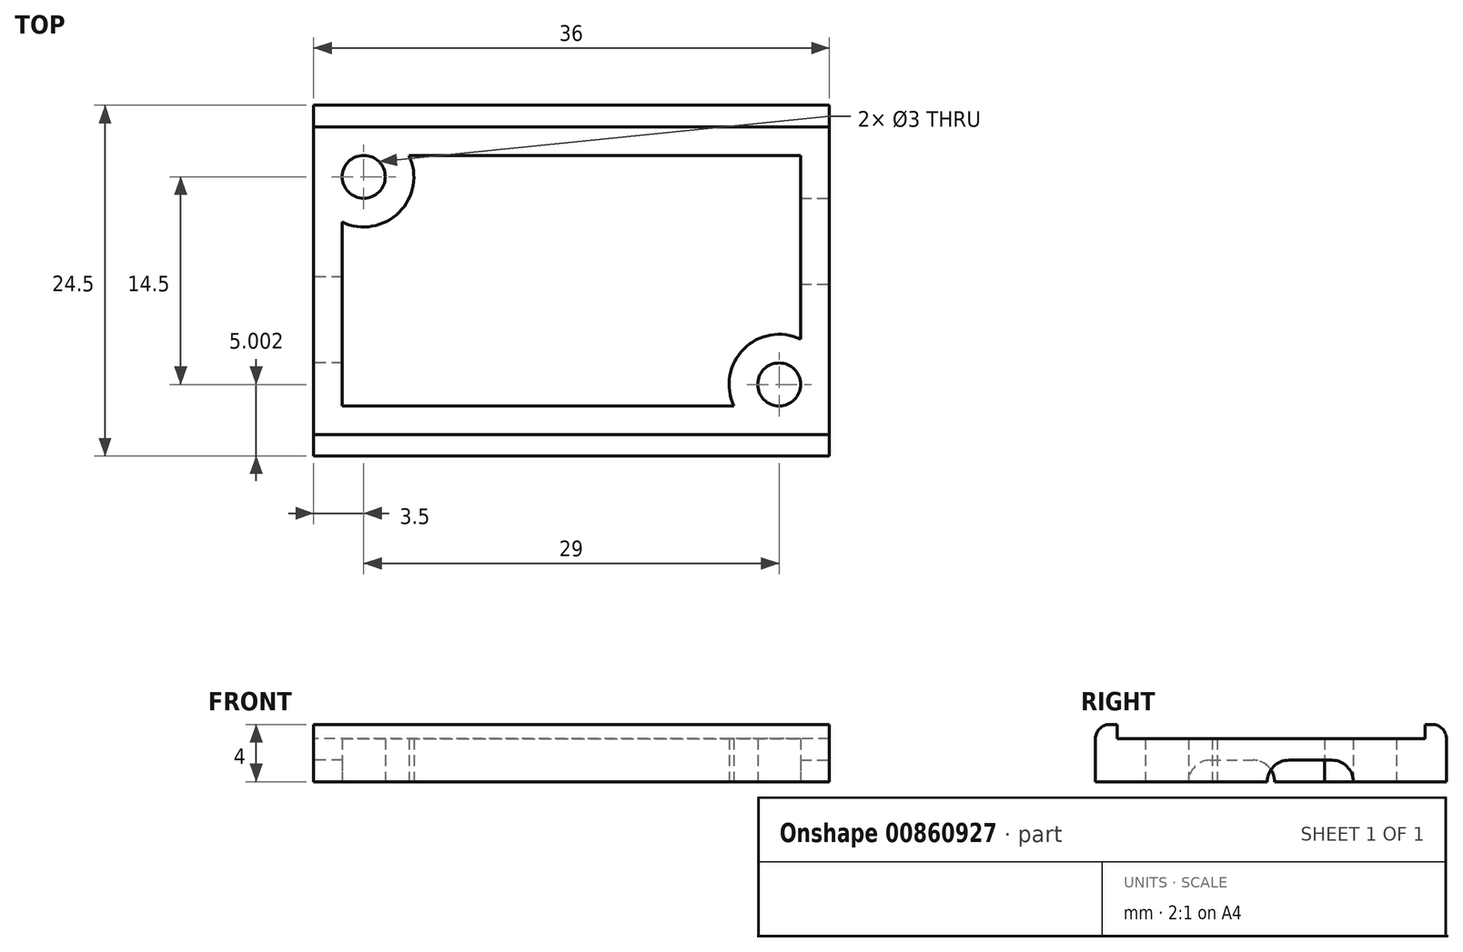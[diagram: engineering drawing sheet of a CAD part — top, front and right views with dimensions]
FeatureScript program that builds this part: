
annotation { "Feature Type Name" : "Feature", "Feature Type Description" : "" }
export const myFeature = defineFeature(function(context is Context, id is Id, definition is map)
    precondition{}
    {
        {
            var Q0;
            Q0=qCreatedBy(makeId("Top.planeOp"),FACE);
            var sketch = newSketch(context, id + "F0", { "sketchPlane" : qUnion([Q0])});
            skLineSegment(sketch, "E0.bottom", {"start": v(-19.82, 7.43) * mm, "end": v(16.18, 7.43) * mm});
            skLineSegment(sketch, "E0.top", {"start": v(-19.82, -14.07) * mm, "end": v(16.18, -14.07) * mm});
            skLineSegment(sketch, "E0.left", {"start": v(-19.82, 7.43) * mm, "end": v(-19.82, -14.07) * mm});
            skLineSegment(sketch, "E0.right", {"start": v(16.18, 7.43) * mm, "end": v(16.18, -14.07) * mm});
            skLineSegment(sketch, "E1.bottom", {"start": v(-19.82, 8.93) * mm, "end": v(16.18, 8.93) * mm});
            skLineSegment(sketch, "E1.top", {"start": v(-19.82, -15.57) * mm, "end": v(16.18, -15.57) * mm});
            skLineSegment(sketch, "E1.left", {"start": v(-19.82, 8.93) * mm, "end": v(-19.82, -15.57) * mm});
            skLineSegment(sketch, "E1.right", {"start": v(16.18, 8.93) * mm, "end": v(16.18, -15.57) * mm});
            skLineSegment(sketch, "E2.bottom", {"start": v(-13.16, 5.43) * mm, "end": v(14.18, 5.43) * mm});
            skLineSegment(sketch, "E2.top", {"start": v(-17.82, -12.07) * mm, "end": v(9.52, -12.07) * mm});
            skLineSegment(sketch, "E2.left", {"start": v(-17.82, 0.77) * mm, "end": v(-17.82, -12.07) * mm});
            skLineSegment(sketch, "E2.right", {"start": v(14.18, 5.43) * mm, "end": v(14.18, -7.4) * mm});
            skPoint(sketch, "E3", {"position": v(-16.32, 3.93) * mm});
            skPoint(sketch, "E4", {"position": v(12.68, -10.57) * mm});
            skArc(sketch, "E5", {"start": v(-17.82, 0.77) * mm, "mid": v(-13.84, 1.46) * mm, "end": v(-13.16, 5.43) * mm});
            skArc(sketch, "E6", {"start": v(14.18, -7.4) * mm, "mid": v(10.2, -8.1) * mm, "end": v(9.52, -12.07) * mm});
            skSolve(sketch);
        }
        {
            var Q0;
            Q0 = qSketchRegion(id + "F0", true);
            extrude(context, id + "F1", {"entities" : qUnion([Q0]), "depth" : 3 * mm, "offsetDistance" : 25 * mm});
        }
        {
            var Q0;
            {var subQ0=sQuery(id+"F0.wireOp",EDGE,"E0.bottom");Q0=makeQuery(id+"F0.imprint","IMPRINT",FACE,{"disambiguationData":[TD([[makeQuery(id+"F0.imprint","IMPRINT",EDGE,{"derivedFrom":subQ0}),1.0]])]});}
            var Q1;
            {var subQ0=sQuery(id+"F0.wireOp",EDGE,"E0.top");Q1=makeQuery(id+"F0.imprint","IMPRINT",FACE,{"disambiguationData":[TD([[makeQuery(id+"F0.imprint","IMPRINT",EDGE,{"derivedFrom":subQ0}),-1.0]])]});}
            extrude(context, id + "F2", {"entities" : qUnion([Q0, Q1]), "operationType" : NewBodyOperationType.ADD, "depth" : 4 * mm, "offsetDistance" : 25 * mm});
        }
        {
            var Q0;
            Q0=sQuery(id+"F0.wireOp",VERTEX,"E4");
            var Q1;
            Q1=sQuery(id+"F0.wireOp",VERTEX,"E3");
            var Q2;
            Q2=makeQuery(id+"F1.opExtrude","SWEPT_BODY",BODY,{"disambiguationData":[OSD([sQuery(id+"F0.wireOp",EDGE,"E1.bottom"),sQuery(id+"F0.wireOp",EDGE,"E1.top"),sQuery(id+"F0.wireOp",EDGE,"E1.left"),sQuery(id+"F0.wireOp",EDGE,"E1.right"),sQuery(id+"F0.wireOp",EDGE,"E2.bottom"),sQuery(id+"F0.wireOp",EDGE,"E2.top"),sQuery(id+"F0.wireOp",EDGE,"E2.left"),sQuery(id+"F0.wireOp",EDGE,"E2.right"),sQuery(id+"F0.wireOp",EDGE,"E5"),sQuery(id+"F0.wireOp",EDGE,"E6")])]});
            hole(context, id + "F3", {"style" : HoleStyle.SIMPLE, "endStyle" : HoleEndStyle.BLIND, "oppositeDirection" : true, "holeDiameter" : 3 * mm, "majorDiameter" : 5 * mm, "holeDepth" : 8 * mm, "isTappedThrough" : true, "tappedDepth" : 12 * mm, "tapClearance" : 3, "startFromSketch" : true, "locations" : qUnion([Q0, Q1]), "scope" : qUnion([Q2])});
        }
        {
            var Q0;
            Q0=makeQuery(id+"F2.opExtrude","CAP_EDGE",EDGE,{"disambiguationData":[OSD([sQuery(id+"F0.wireOp",EDGE,"E1.bottom")])],"isStart":false});
            var Q1;
            Q1=makeQuery(id+"F2.opExtrude","CAP_EDGE",EDGE,{"disambiguationData":[OSD([sQuery(id+"F0.wireOp",EDGE,"E1.top")])],"isStart":false});
            fillet(context, id + "F4", {"entities" : qUnion([Q0, Q1]), "radius" : 1 * mm, "tangentPropagation" : true, "allowEdgeOverflow" : false});
        }
        {
            var Q0;
            {var subQ0=sQuery(id+"F0.wireOp",EDGE,"E1.left");Q0=makeQuery(id+"F2.boolean.opBoolean","MERGE",FACE,{"derivedFrom":[makeQuery(id+"F1.opExtrude","SWEPT_FACE",FACE,{"disambiguationData":[OSD([subQ0])]}),makeQuery(id+"F2.opExtrude","SWEPT_FACE",FACE,{"disambiguationData":[OSD([subQ0]),TDD([makeQuery(id+"F0.imprint","IMPRINT",EDGE,{"disambiguationData":[TD([[makeQuery(id+"F0.imprint","INTERSECT",VERTEX,{"derivedFrom":[sQuery(id+"F0.wireOp",EDGE,"E0.bottom"),subQ0]}),1.0]])],"derivedFrom":subQ0})])]}),makeQuery(id+"F2.opExtrude","SWEPT_FACE",FACE,{"disambiguationData":[OSD([subQ0]),TDD([makeQuery(id+"F0.imprint","IMPRINT",EDGE,{"disambiguationData":[TD([[makeQuery(id+"F0.imprint","INTERSECT",VERTEX,{"derivedFrom":[sQuery(id+"F0.wireOp",EDGE,"E0.top"),subQ0]}),-1.0]])],"derivedFrom":subQ0})])]})]});}
            var sketch = newSketch(context, id + "F5", { "sketchPlane" : qUnion([Q0])});
            skArc(sketch, "E7", {"start": v(4.57, 1.5) * mm, "mid": v(3.12, -0.39) * mm, "end": v(5.32, -1.3) * mm});
            skArc(sketch, "E8", {"start": v(5.32, -1.3) * mm, "mid": v(6.07, -1.5) * mm, "end": v(6.82, -1.3) * mm});
            skArc(sketch, "E9", {"start": v(6.82, -1.3) * mm, "mid": v(9.02, -0.39) * mm, "end": v(7.57, 1.5) * mm});
            skLineSegment(sketch, "E10", {"start": v(4.57, 1.5) * mm, "end": v(7.57, 1.5) * mm});
            skSolve(sketch);
        }
        {
            var Q0;
            Q0 = qSketchRegion(id + "F5", true);
            extrude(context, id + "F6", {"entities" : qUnion([Q0]), "operationType" : NewBodyOperationType.REMOVE, "oppositeDirection" : true, "depth" : 25 * mm, "offsetDistance" : 25 * mm});
        }
        {
            var Q0;
            {var subQ0=sQuery(id+"F0.wireOp",EDGE,"E1.right");Q0=makeQuery(id+"F2.boolean.opBoolean","MERGE",FACE,{"derivedFrom":[makeQuery(id+"F1.opExtrude","SWEPT_FACE",FACE,{"disambiguationData":[OSD([subQ0])]}),makeQuery(id+"F2.opExtrude","SWEPT_FACE",FACE,{"disambiguationData":[OSD([subQ0]),TDD([makeQuery(id+"F0.imprint","IMPRINT",EDGE,{"disambiguationData":[TD([[makeQuery(id+"F0.imprint","INTERSECT",VERTEX,{"derivedFrom":[sQuery(id+"F0.wireOp",EDGE,"E0.bottom"),subQ0]}),1.0]])],"derivedFrom":subQ0})])]}),makeQuery(id+"F2.opExtrude","SWEPT_FACE",FACE,{"disambiguationData":[OSD([subQ0]),TDD([makeQuery(id+"F0.imprint","IMPRINT",EDGE,{"disambiguationData":[TD([[makeQuery(id+"F0.imprint","INTERSECT",VERTEX,{"derivedFrom":[sQuery(id+"F0.wireOp",EDGE,"E0.top"),subQ0]}),-1.0]])],"derivedFrom":subQ0})])]})]});}
            var sketch = newSketch(context, id + "F7", { "sketchPlane" : qUnion([Q0])});
            skCircle(sketch, "E11", {"center": v(0.93, 0) * mm, "radius": 1.5 * mm});
            skCircle(sketch, "E12", {"center": v(-2.07, 0) * mm, "radius": 1.5 * mm});
            skLineSegment(sketch, "E13", {"start": v(-2.07, 1.5) * mm, "end": v(0.93, 1.5) * mm});
            skSolve(sketch);
        }
        {
            var Q0;
            Q0 = qSketchRegion(id + "F7", true);
            extrude(context, id + "F8", {"entities" : qUnion([Q0]), "operationType" : NewBodyOperationType.REMOVE, "oppositeDirection" : true, "depth" : 25 * mm, "offsetDistance" : 25 * mm});
        }
    });
